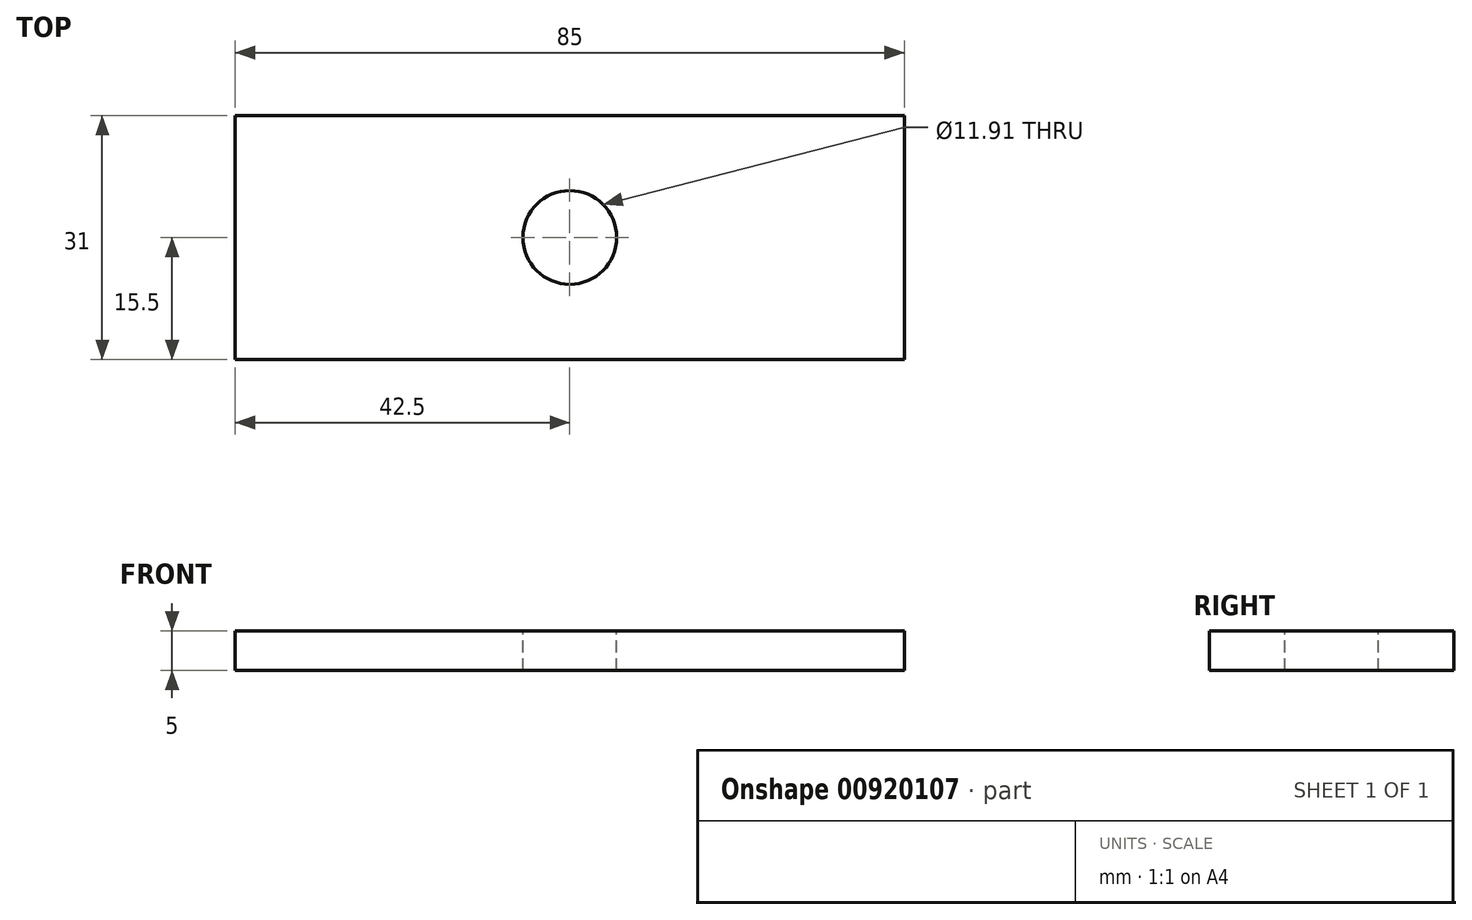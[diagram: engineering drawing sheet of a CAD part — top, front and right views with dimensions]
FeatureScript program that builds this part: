
annotation { "Feature Type Name" : "Feature", "Feature Type Description" : "" }
export const myFeature = defineFeature(function(context is Context, id is Id, definition is map)
    precondition{}
    {
        {
            var Q0;
            Q0=qCreatedBy(makeId("Top.planeOp"),FACE);
            var sketch = newSketch(context, id + "F0", { "sketchPlane" : qUnion([Q0])});
            skLineSegment(sketch, "E0.bottom", {"start": v(0, 0) * mm, "end": v(85, 0) * mm});
            skLineSegment(sketch, "E0.top", {"start": v(0, 31) * mm, "end": v(85, 31) * mm});
            skLineSegment(sketch, "E0.left", {"start": v(0, 0) * mm, "end": v(0, 31) * mm});
            skLineSegment(sketch, "E0.right", {"start": v(85, 0) * mm, "end": v(85, 31) * mm});
            skSolve(sketch);
        }
        {
            var Q0;
            Q0=makeQuery(id+"F0.imprint","IMPRINT",FACE,{"disambiguationData":[TD([[makeQuery(id+"F0.imprint","IMPRINT",EDGE,{"derivedFrom":sQuery(id+"F0.wireOp",EDGE,"E0.bottom")}),1.0]])]});
            extrude(context, id + "F1", {"entities" : qUnion([Q0]), "depth" : 5 * mm, "offsetDistance" : 25 * mm});
        }
        {
            var Q0;
            Q0=makeQuery(id+"F1.opExtrude","CAP_FACE",FACE,{"disambiguationData":[OSD([sQuery(id+"F0.wireOp",EDGE,"E0.bottom"),sQuery(id+"F0.wireOp",EDGE,"E0.top"),sQuery(id+"F0.wireOp",EDGE,"E0.left"),sQuery(id+"F0.wireOp",EDGE,"E0.right")])],"isStart":false});
            var sketch = newSketch(context, id + "F2", { "sketchPlane" : qUnion([Q0])});
            skCircle(sketch, "E1", {"center": v(42.5, 15.5) * mm, "radius": 5.5 * mm});
            skSolve(sketch);
        }
        {
            var Q0;
            Q0=sQuery(id+"F2.wireOp",VERTEX,"E1.center");
            var Q1;
            Q1=makeQuery(id+"F1.opExtrude","SWEPT_BODY",BODY,{"disambiguationData":[OSD([sQuery(id+"F0.wireOp",EDGE,"E0.bottom"),sQuery(id+"F0.wireOp",EDGE,"E0.top"),sQuery(id+"F0.wireOp",EDGE,"E0.left"),sQuery(id+"F0.wireOp",EDGE,"E0.right")])]});
            hole(context, id + "F3", {"style" : HoleStyle.SIMPLE, "endStyle" : HoleEndStyle.THROUGH, "standardTappedOrClearance" : lookupTablePath({ "fit" : "Normal (ASME)", "standard" : "ANSI", "size" : "7/16", "type" : "Clearance" }), "standardBlindInLast" : lookupTablePath({ "fit" : "Normal", "standard" : "ANSI", "size" : "7/16", "type" : "Clearance" }), "holeDiameter" : 11.9 * mm, "majorDiameter" : 11.1 * mm, "isTappedThrough" : true, "tappedDepth" : 12 * mm, "tapClearance" : 3, "locations" : qUnion([Q0]), "scope" : qUnion([Q1])});
        }
    });
